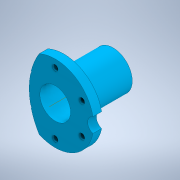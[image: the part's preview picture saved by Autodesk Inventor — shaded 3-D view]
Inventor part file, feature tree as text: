
AUTODESK INVENTOR PART (.ipt)
format: ipt  version: 2022.1 (Build 261234020, 234B)  size: 179,712 bytes
history: native  units: in
note: dims shown in document units (in); Inventor stores cm internally (conversion verified against a paired STEP export)
features: sketch x5, extrude x4, other x3, hole x1, pattern_circular x1, reference x1
ambient origin geometry x8: Origin, YZ Plane, XZ Plane, XY Plane, X Axis, Y Axis, Z Axis, Center Point
bodies: Solid1 (feature_tree)
feature tree (15):
  extrude  "Eyepiece Extrusion"  Depth=1.25in
  extrude  "Bolt Extrusion"  Depth=0.281in TaperAngle=0.0deg
  extrude  "Cutout For Filter Wheel"  Depth=2.5in
  extrude  "Extrusion4"  TaperAngle=0.0deg  [1 undecoded]
  hole  "Hole4"  [1 undecoded]
  pattern_circular  "Circular Pattern2"  [2 undecoded]
  sketch  "Sketch1"  dims[d0=1.25in d1=1.0in]
  sketch  "Sketch2"  dims[d2=1.6in d3=0.0in d4=0.281in d5=0.0in]
  sketch  "Sketch3"  dims[d6=1.0in d7=2.5in]
  reference  "Reference1"
  sketch  "Sketch8"  dims[d8=4.29in d9=0.0in d10=0.0in]
  sketch  "Sketch9"  dims[d50=0.5in d51=1.306in d52=0.0in d53=0.0in d59=1.0in d60=0.185in d61=0.75in d62=0.218in d63=0.2186in d64=0.5635in d65=0.281in d66=0.0in d67=2.3622in d68=360.0deg]
  parser-record x1  (decoder bookkeeping rows leaked as tree rows — omitted from the tree; the rows remain in map.json)
  other  "filterWheelAssembly.iam"
  other  "filterHolder:1"
note: 4 required parameter values undecoded (feature->parameter linkage not recoverable at this tier; creation-order binding heuristic only, values carry confidence <= 0.55)
note: 1 file-system path scrubbed to <path> (originals preserved in map.json)
